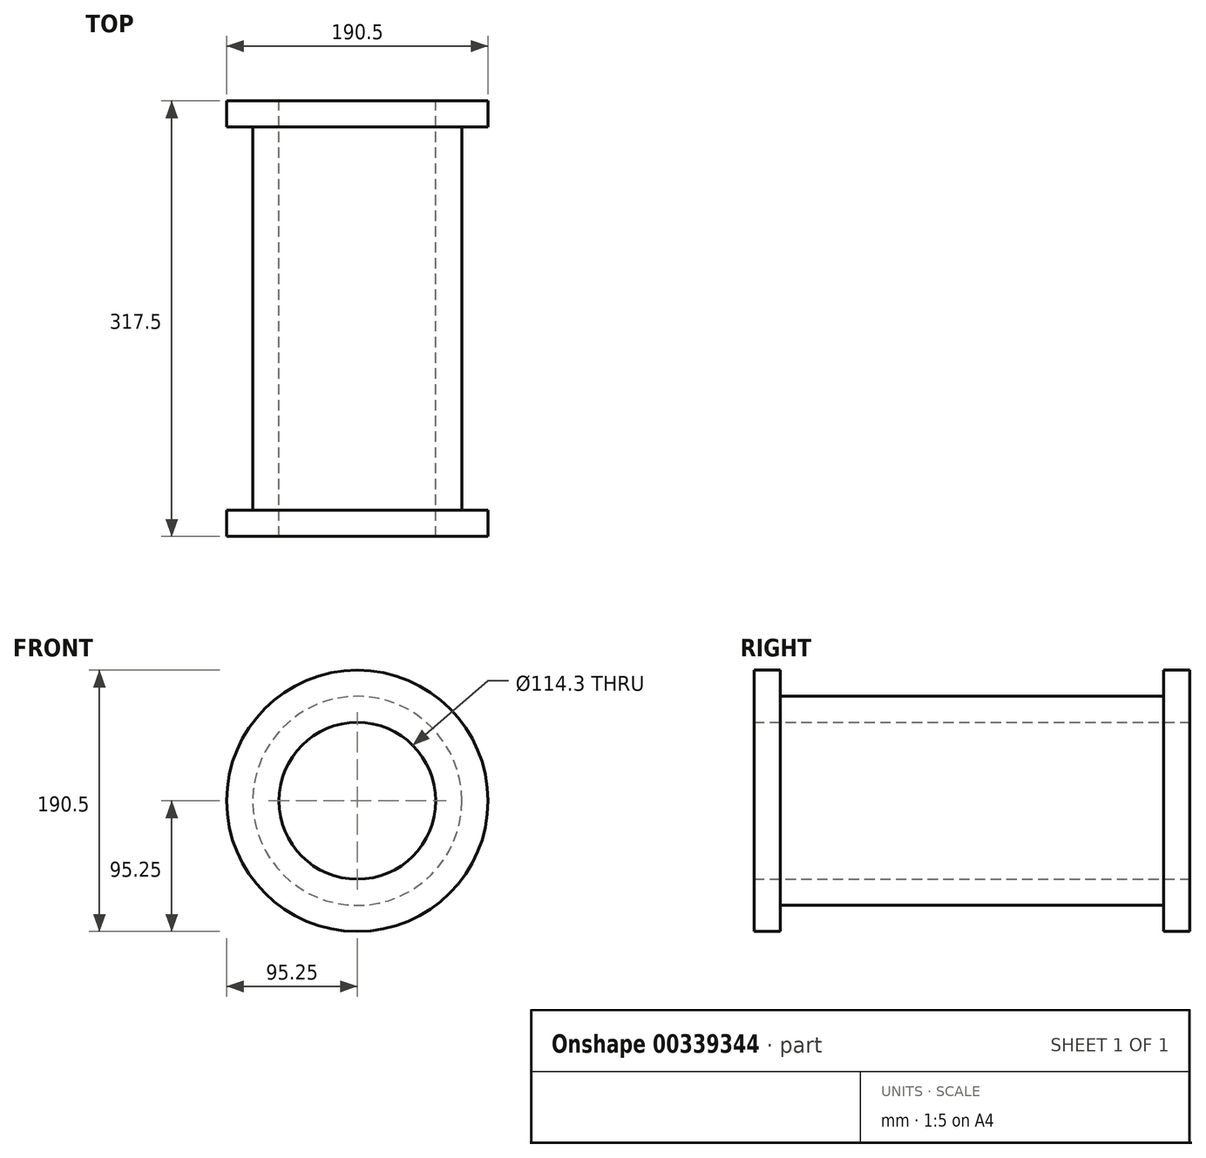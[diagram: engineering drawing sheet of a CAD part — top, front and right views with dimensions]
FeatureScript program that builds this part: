
annotation { "Feature Type Name" : "Feature", "Feature Type Description" : "" }
export const myFeature = defineFeature(function(context is Context, id is Id, definition is map)
    precondition{}
    {
        {
            var Q0;
            Q0=qCreatedBy(makeId("Right.planeOp"),FACE);
            var sketch = newSketch(context, id + "F0", { "sketchPlane" : qUnion([Q0])});
            skLineSegment(sketch, "E0", {"start": v(-52.84, 0) * mm, "end": v(226.56, 0) * mm});
            skSolve(sketch);
        }
        {
            var Q0;
            Q0=sQuery(id+"F0.wireOp",EDGE,"E0");
            var Q1;
            Q1=sQuery(id+"F0.wireOp",VERTEX,"E0.start");
            cPlane(context, id + "F1", {"entities" : qUnion([Q0, Q1]), "cplaneType" : CPlaneType.LINE_POINT, "offset" : 25.4 * mm, "width" : 152.4 * mm, "height" : 152.4 * mm});
        }
        {
            var Q0;
            Q0=qCreatedBy(id+"F1.planeOp",FACE);
            var sketch = newSketch(context, id + "F2", { "sketchPlane" : qUnion([Q0])});
            skCircle(sketch, "E1", {"center": v(0, 0) * mm, "radius": 76.2 * mm});
            skCircle(sketch, "E2", {"center": v(0, 0) * mm, "radius": 95.25 * mm});
            skSolve(sketch);
        }
        {
            var Q0;
            Q0=makeQuery(id+"F2.imprint","IMPRINT",FACE,{"disambiguationData":[TD([[makeQuery(id+"F2.imprint","IMPRINT",EDGE,{"derivedFrom":sQuery(id+"F2.wireOp",EDGE,"E1")}),-1.0]])]});
            var Q1;
            Q1=sQuery(id+"F0.wireOp",EDGE,"E0");
            sweep(context, id + "F3", {"profiles" : qUnion([Q0]), "path" : qUnion([Q1])});
        }
        {
            var Q0;
            Q0=makeQuery(id+"F3.opSweep","SWEPT_FACE",FACE,{"disambiguationData":[OSD([sQuery(id+"F0.wireOp",EDGE,"E0"),sQuery(id+"F2.wireOp",EDGE,"E2")])]});
            shell(context, id + "F4", {"entities" : qUnion([Q0]), "thickness" : 19.05 * mm, "oppositeDirection" : true});
        }
    });
